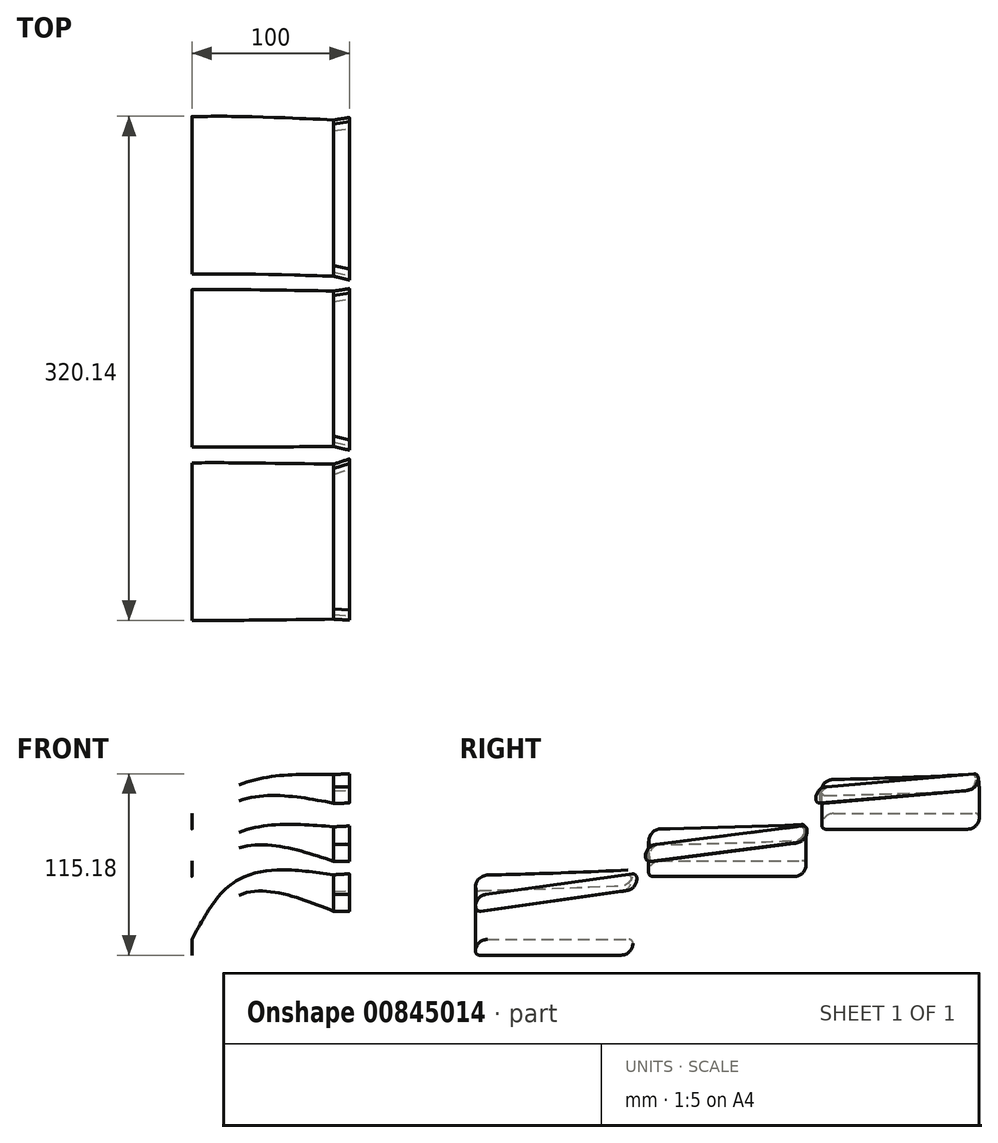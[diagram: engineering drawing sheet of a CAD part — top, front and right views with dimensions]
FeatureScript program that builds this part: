
annotation { "Feature Type Name" : "Feature", "Feature Type Description" : "" }
export const myFeature = defineFeature(function(context is Context, id is Id, definition is map)
    precondition{}
    {
        {
            var Q0;
            Q0=qCreatedBy(makeId("Right.planeOp"),FACE);
            var sketch = newSketch(context, id + "F0", { "sketchPlane" : qUnion([Q0])});
            skLineSegment(sketch, "E0.bottom", {"start": v(-25.4, -25.4) * mm, "end": v(64.6, -25.4) * mm});
            skLineSegment(sketch, "E0.top", {"start": v(-30.4, -35.4) * mm, "end": v(59.6, -35.4) * mm});
            skLineSegment(sketch, "E0.left", {"start": v(-32.9, -32.9) * mm, "end": v(-32.9, -32.9) * mm});
            skLineSegment(sketch, "E0.right", {"start": v(67.1, -27.9) * mm, "end": v(67.1, -27.9) * mm});
            skLineSegment(sketch, "E1.bottom", {"start": v(79.6, 14.6) * mm, "end": v(169.6, 14.6) * mm});
            skLineSegment(sketch, "E1.top", {"start": v(84.6, 24.6) * mm, "end": v(174.6, 24.6) * mm});
            skLineSegment(sketch, "E1.left", {"start": v(77.1, 17.1) * mm, "end": v(77.1, 17.1) * mm});
            skLineSegment(sketch, "E1.right", {"start": v(177.1, 22.1) * mm, "end": v(177.1, 22.1) * mm});
            skLineSegment(sketch, "E2.bottom", {"start": v(189.6, 44.6) * mm, "end": v(279.6, 44.6) * mm});
            skLineSegment(sketch, "E2.top", {"start": v(194.6, 54.6) * mm, "end": v(284.6, 54.6) * mm});
            skLineSegment(sketch, "E2.left", {"start": v(187.1, 47.1) * mm, "end": v(187.1, 47.1) * mm});
            skLineSegment(sketch, "E2.right", {"start": v(287.1, 52.1) * mm, "end": v(287.1, 52.1) * mm});
            skPoint(sketch, "E3.visualSharp", {"position": v(77.1, 24.6) * mm});
            skArc(sketch, "E3.filletArc", {"start": v(84.6, 24.6) * mm, "mid": v(79.3, 22.4) * mm, "end": v(77.1, 17.1) * mm});
            skPoint(sketch, "E4.visualSharp", {"position": v(77.1, 14.6) * mm});
            skArc(sketch, "E4.filletArc", {"start": v(77.1, 17.1) * mm, "mid": v(77.83, 15.33) * mm, "end": v(79.6, 14.6) * mm});
            skPoint(sketch, "E5.visualSharp", {"position": v(177.1, 14.6) * mm});
            skArc(sketch, "E5.filletArc", {"start": v(169.6, 14.6) * mm, "mid": v(174.9, 16.8) * mm, "end": v(177.1, 22.1) * mm});
            skPoint(sketch, "E6.visualSharp", {"position": v(177.1, 24.6) * mm});
            skArc(sketch, "E6.filletArc", {"start": v(177.1, 22.1) * mm, "mid": v(176.37, 23.87) * mm, "end": v(174.6, 24.6) * mm});
            skPoint(sketch, "E7.visualSharp", {"position": v(-32.9, -25.4) * mm});
            skArc(sketch, "E7.filletArc", {"start": v(-25.4, -25.4) * mm, "mid": v(-30.7, -27.6) * mm, "end": v(-32.9, -32.9) * mm});
            skPoint(sketch, "E8.visualSharp", {"position": v(-32.9, -35.4) * mm});
            skArc(sketch, "E8.filletArc", {"start": v(-32.9, -32.9) * mm, "mid": v(-32.17, -34.67) * mm, "end": v(-30.4, -35.4) * mm});
            skPoint(sketch, "E9.visualSharp", {"position": v(67.1, -35.4) * mm});
            skArc(sketch, "E9.filletArc", {"start": v(59.6, -35.4) * mm, "mid": v(64.9, -33.2) * mm, "end": v(67.1, -27.9) * mm});
            skPoint(sketch, "E10.visualSharp", {"position": v(67.1, -25.4) * mm});
            skArc(sketch, "E10.filletArc", {"start": v(67.1, -27.9) * mm, "mid": v(66.37, -26.13) * mm, "end": v(64.6, -25.4) * mm});
            skPoint(sketch, "E11.visualSharp", {"position": v(187.1, 54.6) * mm});
            skArc(sketch, "E11.filletArc", {"start": v(194.6, 54.6) * mm, "mid": v(189.3, 52.4) * mm, "end": v(187.1, 47.1) * mm});
            skPoint(sketch, "E12.visualSharp", {"position": v(187.1, 44.6) * mm});
            skArc(sketch, "E12.filletArc", {"start": v(187.1, 47.1) * mm, "mid": v(187.83, 45.33) * mm, "end": v(189.6, 44.6) * mm});
            skPoint(sketch, "E13.visualSharp", {"position": v(287.1, 54.6) * mm});
            skArc(sketch, "E13.filletArc", {"start": v(287.1, 52.1) * mm, "mid": v(286.37, 53.87) * mm, "end": v(284.6, 54.6) * mm});
            skPoint(sketch, "E14.visualSharp", {"position": v(287.1, 44.6) * mm});
            skArc(sketch, "E14.filletArc", {"start": v(279.6, 44.6) * mm, "mid": v(284.9, 46.8) * mm, "end": v(287.1, 52.1) * mm});
            skSolve(sketch);
        }
        {
            var Q0;
            Q0=qCreatedBy(makeId("Right.planeOp"),FACE);
            cPlane(context, id + "F1", {"entities" : qUnion([Q0]), "cplaneType" : CPlaneType.OFFSET, "offset" : 30 * mm, "width" : 152.4 * mm, "height" : 152.4 * mm});
        }
        {
            var Q0;
            Q0=qCreatedBy(id+"F1.planeOp",FACE);
            var sketch = newSketch(context, id + "F2", { "sketchPlane" : qUnion([Q0])});
            skLineSegment(sketch, "E15.bottom", {"start": v(-25.4, 12.7) * mm, "end": v(64.6, 12.7) * mm});
            skLineSegment(sketch, "E15.top", {"start": v(-30.4, 2.7) * mm, "end": v(59.6, 2.7) * mm});
            skLineSegment(sketch, "E16.bottom", {"start": v(79.6, 32.7) * mm, "end": v(169.6, 32.7) * mm});
            skLineSegment(sketch, "E16.top", {"start": v(84.6, 42.7) * mm, "end": v(174.6, 42.7) * mm});
            skLineSegment(sketch, "E17.bottom", {"start": v(189.6, 62.7) * mm, "end": v(279.6, 62.7) * mm});
            skLineSegment(sketch, "E17.top", {"start": v(194.6, 72.7) * mm, "end": v(284.6, 72.7) * mm});
            skPoint(sketch, "E18.visualSharp", {"position": v(77.1, 42.7) * mm});
            skArc(sketch, "E18.filletArc", {"start": v(84.6, 42.7) * mm, "mid": v(79.3, 40.5) * mm, "end": v(77.1, 35.2) * mm});
            skPoint(sketch, "E19.visualSharp", {"position": v(77.1, 32.7) * mm});
            skArc(sketch, "E19.filletArc", {"start": v(77.1, 35.2) * mm, "mid": v(77.83, 33.43) * mm, "end": v(79.6, 32.7) * mm});
            skPoint(sketch, "E20.visualSharp", {"position": v(177.1, 32.7) * mm});
            skArc(sketch, "E20.filletArc", {"start": v(169.6, 32.7) * mm, "mid": v(174.9, 34.9) * mm, "end": v(177.1, 40.2) * mm});
            skPoint(sketch, "E21.visualSharp", {"position": v(177.1, 42.7) * mm});
            skArc(sketch, "E21.filletArc", {"start": v(177.1, 40.2) * mm, "mid": v(176.37, 41.97) * mm, "end": v(174.6, 42.7) * mm});
            skPoint(sketch, "E22.visualSharp", {"position": v(-32.9, 12.7) * mm});
            skArc(sketch, "E22.filletArc", {"start": v(-25.4, 12.7) * mm, "mid": v(-30.7, 10.5) * mm, "end": v(-32.9, 5.2) * mm});
            skPoint(sketch, "E23.visualSharp", {"position": v(-32.9, 2.7) * mm});
            skArc(sketch, "E23.filletArc", {"start": v(-32.9, 5.2) * mm, "mid": v(-32.17, 3.43) * mm, "end": v(-30.4, 2.7) * mm});
            skPoint(sketch, "E24.visualSharp", {"position": v(67.1, 2.7) * mm});
            skArc(sketch, "E24.filletArc", {"start": v(59.6, 2.7) * mm, "mid": v(64.9, 4.9) * mm, "end": v(67.1, 10.2) * mm});
            skPoint(sketch, "E25.visualSharp", {"position": v(67.1, 12.7) * mm});
            skArc(sketch, "E25.filletArc", {"start": v(67.1, 10.2) * mm, "mid": v(66.37, 11.97) * mm, "end": v(64.6, 12.7) * mm});
            skPoint(sketch, "E26.visualSharp", {"position": v(187.1, 72.7) * mm});
            skArc(sketch, "E26.filletArc", {"start": v(194.6, 72.7) * mm, "mid": v(189.3, 70.5) * mm, "end": v(187.1, 65.2) * mm});
            skPoint(sketch, "E27.visualSharp", {"position": v(187.1, 62.7) * mm});
            skArc(sketch, "E27.filletArc", {"start": v(187.1, 65.2) * mm, "mid": v(187.83, 63.43) * mm, "end": v(189.6, 62.7) * mm});
            skPoint(sketch, "E28.visualSharp", {"position": v(287.1, 72.7) * mm});
            skArc(sketch, "E28.filletArc", {"start": v(287.1, 70.2) * mm, "mid": v(286.37, 71.97) * mm, "end": v(284.6, 72.7) * mm});
            skPoint(sketch, "E29.visualSharp", {"position": v(287.1, 62.7) * mm});
            skArc(sketch, "E29.filletArc", {"start": v(279.6, 62.7) * mm, "mid": v(284.9, 64.9) * mm, "end": v(287.1, 70.2) * mm});
            skSolve(sketch);
        }
        {
            var Q0;
            Q0=qCreatedBy(id+"F1.planeOp",FACE);
            cPlane(context, id + "F3", {"entities" : qUnion([Q0]), "cplaneType" : CPlaneType.OFFSET, "offset" : 60 * mm, "width" : 152.4 * mm, "height" : 152.4 * mm});
        }
        {
            var Q0;
            Q0=qCreatedBy(id+"F3.planeOp",FACE);
            var sketch = newSketch(context, id + "F4", { "sketchPlane" : qUnion([Q0])});
            skLineSegment(sketch, "E30.bottom", {"start": v(-25.77, 3.15) * mm, "end": v(63.36, 15.65) * mm});
            skLineSegment(sketch, "E30.top", {"start": v(-29.33, -7.45) * mm, "end": v(59.8, 5.05) * mm});
            skLineSegment(sketch, "E31.bottom", {"start": v(80.35, 24.27) * mm, "end": v(169.63, 35.56) * mm});
            skLineSegment(sketch, "E31.top", {"start": v(84.05, 34.81) * mm, "end": v(173.34, 46.1) * mm});
            skLineSegment(sketch, "E32.bottom", {"start": v(188.36, 61.15) * mm, "end": v(278.02, 69) * mm});
            skLineSegment(sketch, "E32.top", {"start": v(192.47, 71.55) * mm, "end": v(282.13, 79.4) * mm});
            skPoint(sketch, "E33.visualSharp", {"position": v(76.61, 33.87) * mm});
            skArc(sketch, "E33.filletArc", {"start": v(84.05, 34.81) * mm, "mid": v(79.07, 31.97) * mm, "end": v(77.55, 26.43) * mm});
            skPoint(sketch, "E34.visualSharp", {"position": v(77.86, 23.95) * mm});
            skArc(sketch, "E34.filletArc", {"start": v(77.55, 26.43) * mm, "mid": v(78.5, 24.77) * mm, "end": v(80.35, 24.27) * mm});
            skPoint(sketch, "E35.visualSharp", {"position": v(177.07, 36.5) * mm});
            skArc(sketch, "E35.filletArc", {"start": v(169.63, 35.56) * mm, "mid": v(174.62, 38.4) * mm, "end": v(176.13, 43.94) * mm});
            skPoint(sketch, "E36.visualSharp", {"position": v(175.82, 46.42) * mm});
            skArc(sketch, "E36.filletArc", {"start": v(176.13, 43.94) * mm, "mid": v(175.19, 45.6) * mm, "end": v(173.34, 46.1) * mm});
            skPoint(sketch, "E37.visualSharp", {"position": v(-33.2, 2.1) * mm});
            skArc(sketch, "E37.filletArc", {"start": v(-25.77, 3.15) * mm, "mid": v(-30.71, 0.24) * mm, "end": v(-32.15, -5.32) * mm});
            skPoint(sketch, "E38.visualSharp", {"position": v(-31.8, -7.8) * mm});
            skArc(sketch, "E38.filletArc", {"start": v(-32.15, -5.32) * mm, "mid": v(-31.18, -6.97) * mm, "end": v(-29.33, -7.45) * mm});
            skPoint(sketch, "E39.visualSharp", {"position": v(67.22, 6.1) * mm});
            skArc(sketch, "E39.filletArc", {"start": v(59.8, 5.05) * mm, "mid": v(64.74, 7.97) * mm, "end": v(66.18, 13.52) * mm});
            skPoint(sketch, "E40.visualSharp", {"position": v(65.83, 16) * mm});
            skArc(sketch, "E40.filletArc", {"start": v(66.18, 13.52) * mm, "mid": v(65.21, 15.17) * mm, "end": v(63.36, 15.65) * mm});
            skPoint(sketch, "E41.visualSharp", {"position": v(185, 70.9) * mm});
            skArc(sketch, "E41.filletArc", {"start": v(192.47, 71.55) * mm, "mid": v(187.38, 68.9) * mm, "end": v(185.66, 63.42) * mm});
            skPoint(sketch, "E42.visualSharp", {"position": v(185.87, 60.93) * mm});
            skArc(sketch, "E42.filletArc", {"start": v(185.66, 63.42) * mm, "mid": v(186.54, 61.72) * mm, "end": v(188.36, 61.15) * mm});
            skPoint(sketch, "E43.visualSharp", {"position": v(284.62, 79.6) * mm});
            skArc(sketch, "E43.filletArc", {"start": v(284.84, 77.12) * mm, "mid": v(283.96, 78.82) * mm, "end": v(282.13, 79.4) * mm});
            skPoint(sketch, "E44.visualSharp", {"position": v(285.5, 69.65) * mm});
            skArc(sketch, "E44.filletArc", {"start": v(278.02, 69) * mm, "mid": v(283.11, 71.64) * mm, "end": v(284.84, 77.12) * mm});
            skSolve(sketch);
        }
        {
            var Q0;
            Q0=qCreatedBy(id+"F3.planeOp",FACE);
            cPlane(context, id + "F5", {"entities" : qUnion([Q0]), "cplaneType" : CPlaneType.OFFSET, "offset" : 10 * mm, "width" : 152.4 * mm, "height" : 152.4 * mm});
        }
        {
            var Q0;
            Q0=makeQuery(id+"F0.imprint","IMPRINT",FACE,{"disambiguationData":[TD([[makeQuery(id+"F0.imprint","IMPRINT",EDGE,{"derivedFrom":sQuery(id+"F0.wireOp",EDGE,"E0.bottom")}),-1.0]])]});
            var Q1;
            Q1=makeQuery(id+"F2.imprint","IMPRINT",FACE,{"disambiguationData":[TD([[makeQuery(id+"F2.imprint","IMPRINT",EDGE,{"derivedFrom":sQuery(id+"F2.wireOp",EDGE,"E15.bottom")}),-1.0]])]});
            var Q2;
            Q2=makeQuery(id+"F4.imprint","IMPRINT",FACE,{"disambiguationData":[TD([[makeQuery(id+"F4.imprint","IMPRINT",EDGE,{"derivedFrom":sQuery(id+"F4.wireOp",EDGE,"E30.bottom")}),-1.0]])]});
            loft(context, id + "F6", {"sheetProfilesArray" : [{ "sheetProfileEntities" : qUnion([Q0]) }, { "sheetProfileEntities" : qUnion([Q1]) }, { "sheetProfileEntities" : qUnion([Q2]) }]});
        }
        {
            var Q0;
            Q0=makeQuery(id+"F0.imprint","IMPRINT",FACE,{"disambiguationData":[TD([[makeQuery(id+"F0.imprint","IMPRINT",EDGE,{"derivedFrom":sQuery(id+"F0.wireOp",EDGE,"E1.bottom")}),1.0]])]});
            var Q1;
            Q1=makeQuery(id+"F2.imprint","IMPRINT",FACE,{"disambiguationData":[TD([[makeQuery(id+"F2.imprint","IMPRINT",EDGE,{"derivedFrom":sQuery(id+"F2.wireOp",EDGE,"E16.bottom")}),1.0]])]});
            var Q2;
            Q2=makeQuery(id+"F4.imprint","IMPRINT",FACE,{"disambiguationData":[TD([[makeQuery(id+"F4.imprint","IMPRINT",EDGE,{"derivedFrom":sQuery(id+"F4.wireOp",EDGE,"E31.bottom")}),1.0]])]});
            loft(context, id + "F7", {"sheetProfilesArray" : [{ "sheetProfileEntities" : qUnion([Q0]) }, { "sheetProfileEntities" : qUnion([Q1]) }, { "sheetProfileEntities" : qUnion([Q2]) }]});
        }
        {
            var Q0;
            Q0=makeQuery(id+"F0.imprint","IMPRINT",FACE,{"disambiguationData":[TD([[makeQuery(id+"F0.imprint","IMPRINT",EDGE,{"derivedFrom":sQuery(id+"F0.wireOp",EDGE,"E2.bottom")}),1.0]])]});
            var Q1;
            Q1=makeQuery(id+"F2.imprint","IMPRINT",FACE,{"disambiguationData":[TD([[makeQuery(id+"F2.imprint","IMPRINT",EDGE,{"derivedFrom":sQuery(id+"F2.wireOp",EDGE,"E17.bottom")}),1.0]])]});
            var Q2;
            Q2=makeQuery(id+"F4.imprint","IMPRINT",FACE,{"disambiguationData":[TD([[makeQuery(id+"F4.imprint","IMPRINT",EDGE,{"derivedFrom":sQuery(id+"F4.wireOp",EDGE,"E32.bottom")}),1.0]])]});
            loft(context, id + "F8", {"sheetProfilesArray" : [{ "sheetProfileEntities" : qUnion([Q0]) }, { "sheetProfileEntities" : qUnion([Q1]) }, { "sheetProfileEntities" : qUnion([Q2]) }]});
        }
        {
            var Q0;
            Q0=qCreatedBy(id+"F5.planeOp",FACE);
            var sketch = newSketch(context, id + "F9", { "sketchPlane" : qUnion([Q0])});
            skLineSegment(sketch, "E45.bottom", {"start": v(-26.38, 3.18) * mm, "end": v(66.69, 16.23) * mm});
            skLineSegment(sketch, "E45.top", {"start": v(-29.94, -7.42) * mm, "end": v(63.13, 5.63) * mm});
            skLineSegment(sketch, "E46.bottom", {"start": v(77.94, 24.3) * mm, "end": v(171.18, 36.09) * mm});
            skLineSegment(sketch, "E46.top", {"start": v(81.65, 34.84) * mm, "end": v(174.89, 46.64) * mm});
            skLineSegment(sketch, "E47.bottom", {"start": v(185.96, 61.18) * mm, "end": v(279.59, 69.37) * mm});
            skLineSegment(sketch, "E47.top", {"start": v(190.07, 71.58) * mm, "end": v(283.7, 79.77) * mm});
            skPoint(sketch, "E48.visualSharp", {"position": v(74.2, 33.9) * mm});
            skArc(sketch, "E48.filletArc", {"start": v(81.65, 34.84) * mm, "mid": v(76.66, 32) * mm, "end": v(75.15, 26.46) * mm});
            skPoint(sketch, "E49.visualSharp", {"position": v(75.46, 23.98) * mm});
            skArc(sketch, "E49.filletArc", {"start": v(75.15, 26.46) * mm, "mid": v(76.1, 24.8) * mm, "end": v(77.94, 24.3) * mm});
            skPoint(sketch, "E50.visualSharp", {"position": v(174.67, 36.53) * mm});
            skArc(sketch, "E50.filletArc", {"start": v(171.18, 36.09) * mm, "mid": v(176.17, 38.93) * mm, "end": v(177.68, 44.47) * mm});
            skPoint(sketch, "E51.visualSharp", {"position": v(173.42, 46.45) * mm});
            skArc(sketch, "E51.filletArc", {"start": v(177.68, 44.47) * mm, "mid": v(176.73, 46.13) * mm, "end": v(174.89, 46.64) * mm});
            skPoint(sketch, "E52.visualSharp", {"position": v(-33.8, 2.13) * mm});
            skArc(sketch, "E52.filletArc", {"start": v(-26.38, 3.18) * mm, "mid": v(-31.33, 0.26) * mm, "end": v(-32.77, -5.3) * mm});
            skPoint(sketch, "E53.visualSharp", {"position": v(-32.42, -7.77) * mm});
            skArc(sketch, "E53.filletArc", {"start": v(-32.77, -5.3) * mm, "mid": v(-31.8, -6.94) * mm, "end": v(-29.94, -7.42) * mm});
            skPoint(sketch, "E54.visualSharp", {"position": v(66.61, 6.12) * mm});
            skArc(sketch, "E54.filletArc", {"start": v(63.13, 5.63) * mm, "mid": v(68.07, 8.55) * mm, "end": v(69.51, 14.1) * mm});
            skPoint(sketch, "E55.visualSharp", {"position": v(65.22, 16.03) * mm});
            skArc(sketch, "E55.filletArc", {"start": v(69.51, 14.1) * mm, "mid": v(68.54, 15.75) * mm, "end": v(66.69, 16.23) * mm});
            skPoint(sketch, "E56.visualSharp", {"position": v(182.6, 70.92) * mm});
            skArc(sketch, "E56.filletArc", {"start": v(190.07, 71.58) * mm, "mid": v(184.98, 68.92) * mm, "end": v(183.26, 63.45) * mm});
            skPoint(sketch, "E57.visualSharp", {"position": v(183.47, 60.96) * mm});
            skArc(sketch, "E57.filletArc", {"start": v(183.26, 63.45) * mm, "mid": v(184.14, 61.75) * mm, "end": v(185.96, 61.18) * mm});
            skPoint(sketch, "E58.visualSharp", {"position": v(284, 79.64) * mm});
            skArc(sketch, "E58.filletArc", {"start": v(286.4, 77.5) * mm, "mid": v(285.52, 79.2) * mm, "end": v(283.7, 79.77) * mm});
            skPoint(sketch, "E59.visualSharp", {"position": v(283.1, 69.68) * mm});
            skArc(sketch, "E59.filletArc", {"start": v(279.59, 69.37) * mm, "mid": v(284.68, 72.02) * mm, "end": v(286.4, 77.5) * mm});
            skSolve(sketch);
        }
        {
            var Q1;
            Q1=makeQuery(id+"F4.imprint","IMPRINT",FACE,{"disambiguationData":[TD([[makeQuery(id+"F4.imprint","IMPRINT",EDGE,{"derivedFrom":sQuery(id+"F4.wireOp",EDGE,"E32.bottom")}),1.0]])]});
            var Q2;
            Q2=makeQuery(id+"F9.imprint","IMPRINT",FACE,{"disambiguationData":[TD([[makeQuery(id+"F9.imprint","IMPRINT",EDGE,{"derivedFrom":sQuery(id+"F9.wireOp",EDGE,"E47.bottom")}),1.0]])]});
            loft(context, id + "F10", {"operationType" : NewBodyOperationType.ADD, "sheetProfilesArray" : [{ "sheetProfileEntities" : qUnion([Q1]) }, { "sheetProfileEntities" : qUnion([Q2]) }]});
        }
        {
            var Q1;
            Q1=makeQuery(id+"F4.imprint","IMPRINT",FACE,{"disambiguationData":[TD([[makeQuery(id+"F4.imprint","IMPRINT",EDGE,{"derivedFrom":sQuery(id+"F4.wireOp",EDGE,"E31.bottom")}),1.0]])]});
            var Q2;
            Q2=makeQuery(id+"F9.imprint","IMPRINT",FACE,{"disambiguationData":[TD([[makeQuery(id+"F9.imprint","IMPRINT",EDGE,{"derivedFrom":sQuery(id+"F9.wireOp",EDGE,"E46.bottom")}),1.0]])]});
            loft(context, id + "F11", {"operationType" : NewBodyOperationType.ADD, "sheetProfilesArray" : [{ "sheetProfileEntities" : qUnion([Q1]) }, { "sheetProfileEntities" : qUnion([Q2]) }]});
        }
        {
            var Q1;
            Q1=makeQuery(id+"F4.imprint","IMPRINT",FACE,{"disambiguationData":[TD([[makeQuery(id+"F4.imprint","IMPRINT",EDGE,{"derivedFrom":sQuery(id+"F4.wireOp",EDGE,"E30.bottom")}),-1.0]])]});
            var Q2;
            Q2=makeQuery(id+"F9.imprint","IMPRINT",FACE,{"disambiguationData":[TD([[makeQuery(id+"F9.imprint","IMPRINT",EDGE,{"derivedFrom":sQuery(id+"F9.wireOp",EDGE,"E45.bottom")}),-1.0]])]});
            loft(context, id + "F12", {"operationType" : NewBodyOperationType.ADD, "sheetProfilesArray" : [{ "sheetProfileEntities" : qUnion([Q1]) }, { "sheetProfileEntities" : qUnion([Q2]) }]});
        }
        {
            var Q0;
            Q0=qCreatedBy(id+"F5.planeOp",FACE);
            cPlane(context, id + "F13", {"entities" : qUnion([Q0]), "cplaneType" : CPlaneType.OFFSET, "offset" : 40 * mm, "width" : 152.4 * mm, "height" : 152.4 * mm});
        }
    });
